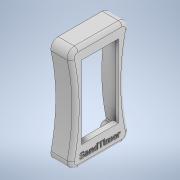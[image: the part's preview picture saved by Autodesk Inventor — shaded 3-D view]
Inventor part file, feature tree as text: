
AUTODESK INVENTOR PART (.ipt)
format: ipt  version: 2021 (Build 250183000, 183)  size: 537,600 bytes
history: native  units: mm
features: extrude x7, sketch x7, fillet x3, mirror x2, shell x1, plane x1, thicken_offset x1, projected_geometry x1
ambient origin geometry x8: Origin, YZ Plane, XZ Plane, XY Plane, X Axis, Y Axis, Z Axis, Center Point
bodies: Solid1 (feature_tree)
feature tree (23):
  extrude  "Extrusion1"  Depth=27.0mm
  extrude  "Extrusion5"  Depth=2.0mm
  fillet  "Fillet1"  Radius=1.5mm
  shell  "Shell1"  Thickness=3.8mm
  extrude  "Extrusion9"  Depth=4.0mm
  extrude  "Extrusion12"  Depth=41.0mm
  extrude  "Extrusion17"  TaperAngle=0.0deg  [1 undecoded]
  fillet  "Fillet13"  Radius=24.0mm
  extrude  "Extrusion18"  Depth=3.0mm
  mirror  "Mirror9"
  plane  "Work Plane8"
  mirror  "Mirror10"
  thicken_offset  "Thicken1"
  extrude  "Extrusion19"  Depth=1.0mm
  fillet  "Fillet14"  Radius=1.9mm
  sketch  "Sketch1"  dims[d0=11.0mm d1=27.0mm]
  sketch  "Sketch5"  dims[d2=58.0mm d3=0.0mm d4=2.0mm d5=1.5mm d26=3.8mm]
  sketch  "Sketch9"  dims[d27=0.0mm d28=0.0mm d29=4.0mm]
  sketch  "Sketch12"  dims[d53=21.0mm d54=41.0mm]
  sketch  "Sketch17"  dims[d55=6.54mm d56=0.0mm d57=0.0mm d68=24.0mm]
  sketch  "Sketch18"  dims[d69=4.0mm d70=3.0mm]
  sketch  "Sketch19"  dims[d71=0.5mm d72=0.0mm d99=1.0mm d106=1.9mm d107=4.0mm d110=4.0mm d111=0.0mm d112=0.5mm d113=4.0mm d114=0.0mm d115=1.5mm d116=0.25mm d117=0.25mm d118=1.5mm d119=1.5mm d120=1.5mm d121=0.0mm d122=0.5mm]
  projected_geometry  "Project Cut Edges12"
note: 1 required parameter value undecoded (feature->parameter linkage not recoverable at this tier; creation-order binding heuristic only, values carry confidence <= 0.55)
